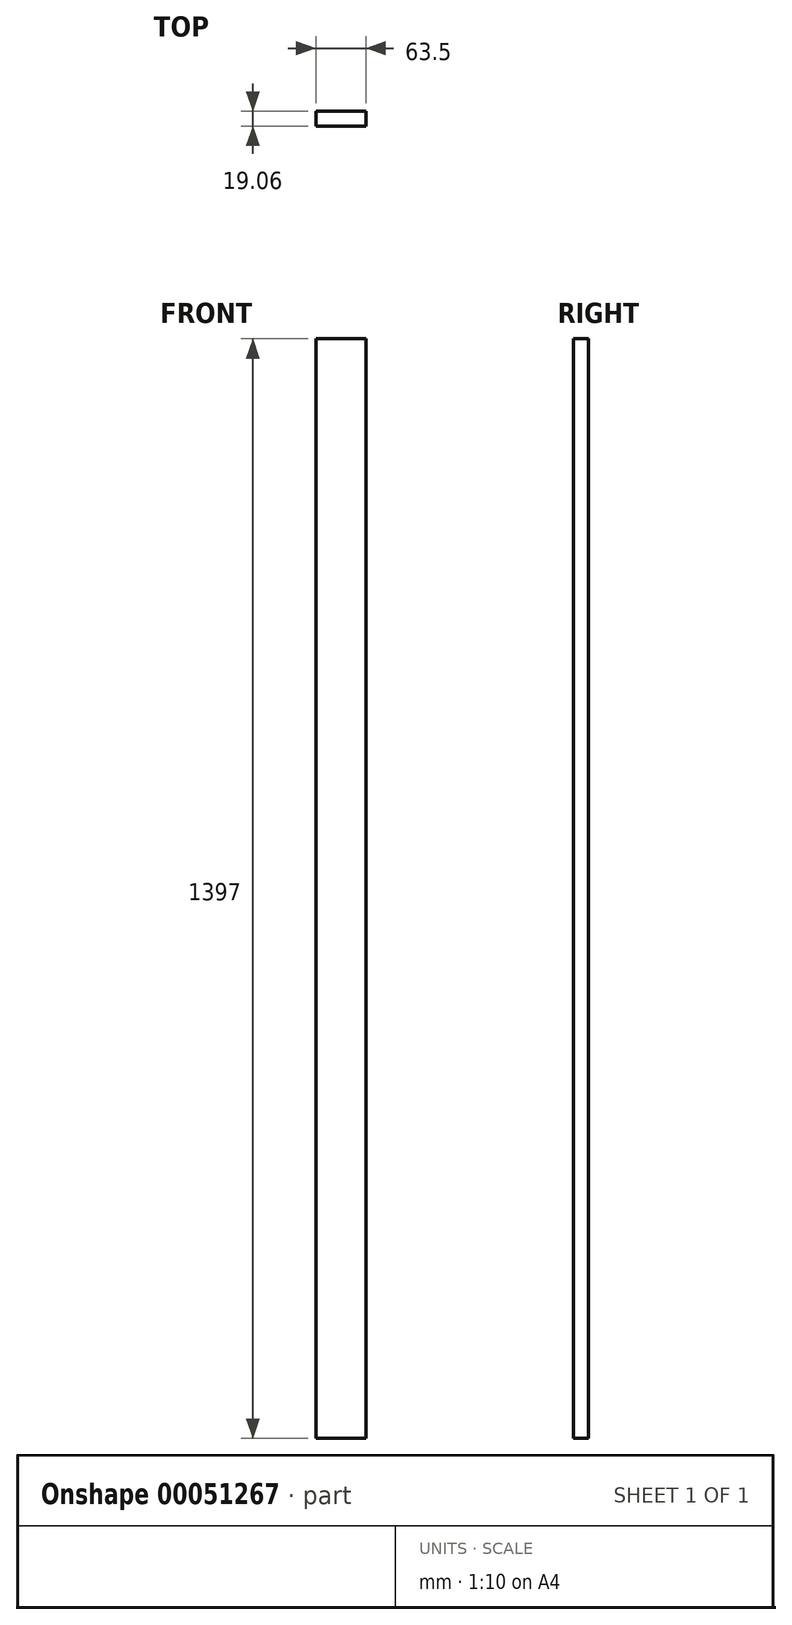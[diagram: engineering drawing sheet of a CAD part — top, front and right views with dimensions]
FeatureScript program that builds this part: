
annotation { "Feature Type Name" : "Feature", "Feature Type Description" : "" }
export const myFeature = defineFeature(function(context is Context, id is Id, definition is map)
    precondition{}
    {
        {
            var Q0;
            Q0=qCreatedBy(makeId("Top.planeOp"),FACE);
            var sketch = newSketch(context, id + "F0", { "sketchPlane" : qUnion([Q0])});
            skLineSegment(sketch, "E0.rect.bottom", {"start": v(31.75, 9.53) * mm, "end": v(-31.75, 9.53) * mm});
            skLineSegment(sketch, "E0.rect.top", {"start": v(31.75, -9.52) * mm, "end": v(-31.75, -9.52) * mm});
            skLineSegment(sketch, "E0.rect.left", {"start": v(31.75, 9.53) * mm, "end": v(31.75, -9.52) * mm});
            skLineSegment(sketch, "E0.rect.right", {"start": v(-31.75, 9.53) * mm, "end": v(-31.75, -9.52) * mm});
            skPoint(sketch, "E0.rect.middle", {"position": v(0, 0) * mm});
            skSolve(sketch);
        }
        {
            var Q0;
            Q0 = qSketchRegion(id + "F0", true);
            extrude(context, id + "F1", {"entities" : qUnion([Q0]), "endBound" : BoundingType.SYMMETRIC, "depth" : 1397 * mm});
        }
    });
